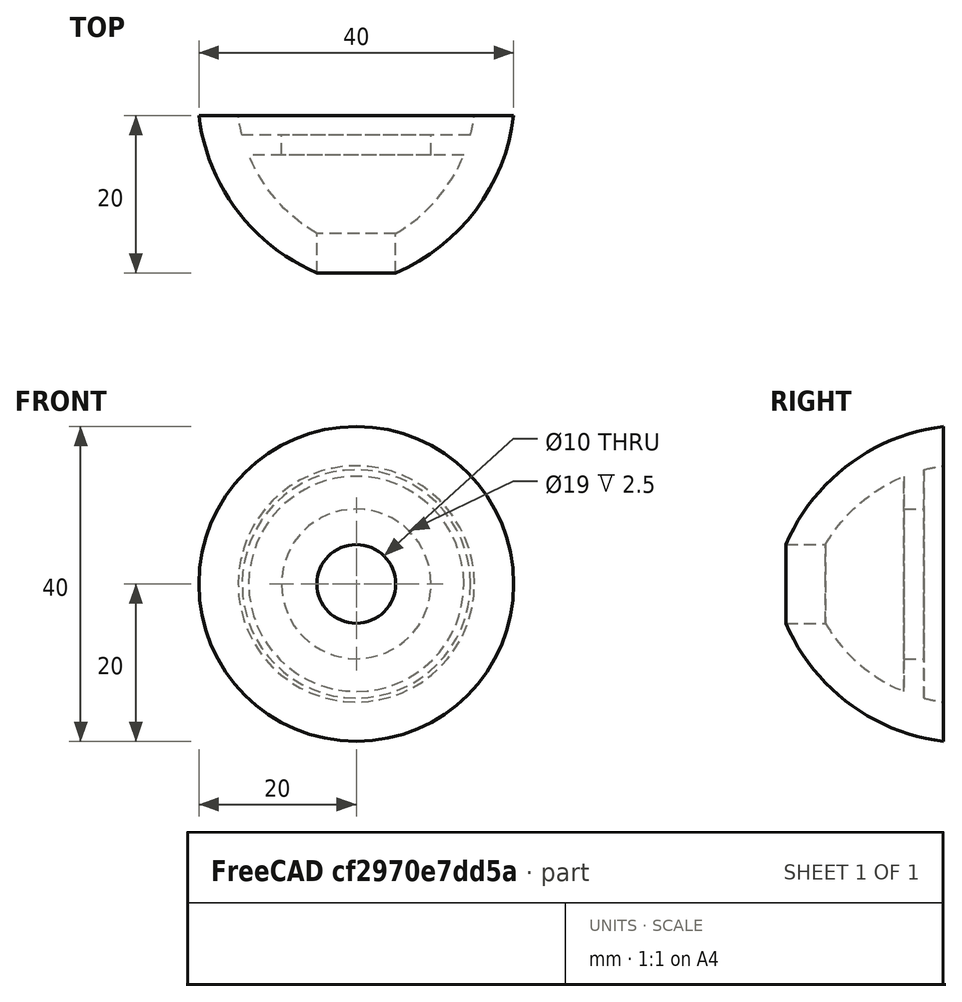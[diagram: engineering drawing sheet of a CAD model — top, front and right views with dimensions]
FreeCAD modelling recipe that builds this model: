
FCSTD DOCUMENT  (FreeCAD 0.18R4 (GitTag))
Label: Ariel Reciever
License: All rights reserved
LicenseURL: http://en.wikipedia.org/wiki/All_rights_reserved
objects: Sketcher::SketchObject×1, PartDesign::Revolution×1, PartDesign::Body×1, Mesh::Feature×1
note: 4 computed .brp shape members not serialized (recipe doc carries the construction recipe); baked Part::Feature solids carry a one-line shape summary decoded from their .brp

FEATURE [Sketcher::SketchObject] Sketch
  MapMode = 5
  Support = -> [XY_Plane]
  sketch-geometry (12):
    g0: ArcOfCircle CenterX=-4.82051 CenterY=22.9904 CenterZ=0 NormalX=0 NormalY=0 NormalZ=1 AngleXU=0 Radius=25 StartAngle=5.11609 EndAngle=6.16328
    g1: LineSegment StartX=5 StartY=-3.6e-15 StartZ=0 EndX=5 EndY=5 EndZ=0
    g2: LineSegment StartX=20 StartY=20 StartZ=0 EndX=15 EndY=20 EndZ=0
    g3: LineSegment [constr] StartX=0 StartY=26.4416 StartZ=0 EndX=26.4416 EndY=0 EndZ=0
    g4: GeomPoint X=12.9669 Y=13.4747 Z=0
    g5: GeomPoint X=16.5024 Y=9.93921 Z=0
    g6: LineSegment StartX=13.6625 StartY=15 StartZ=0 EndX=9.5 EndY=15 EndZ=0
    g7: LineSegment StartX=9.5 StartY=15 StartZ=0 EndX=9.5 EndY=17.5 EndZ=0
    g8: LineSegment StartX=9.5 StartY=17.5 StartZ=0 EndX=14.5 EndY=17.5 EndZ=0
    g9: ArcOfCircle [constr] CenterX=-5.42857 CenterY=22.7857 CenterZ=0 NormalX=0 NormalY=0 NormalZ=1 AngleXU=0 Radius=20.6176 StartAngle=5.24271 EndAngle=6.14766
    g10: ArcOfCircle CenterX=-5.42857 CenterY=22.7857 CenterZ=0 NormalX=0 NormalY=0 NormalZ=1 AngleXU=0 Radius=20.6176 StartAngle=5.24271 EndAngle=5.89596
    g11: ArcOfCircle CenterX=-5.42857 CenterY=22.7857 CenterZ=0 NormalX=0 NormalY=0 NormalZ=1 AngleXU=0 Radius=20.6176 StartAngle=6.02392 EndAngle=6.14766
  constraints (38):
    c: PointOnObject(g0,g-1)
    c: DistanceX(g-1,g0) = 5
    c: Radius(g0) = 25
    c: DistanceX(g-1,g0) = 20
    c: DistanceY(g-1,g0) = 20
    c: Coincident(g1,g0)
    c: Vertical(g1)
    c: Coincident(g2,g0)
    c: Horizontal(g2)
    c: DistanceX(g2,g2) = 5
    c: DistanceY(g1,g1) = 5
    c: PointOnObject(g3,g-2)
    c: PointOnObject(g3,g-1)
    c: Angle(g3,g-1) = 0.785398
    c: PointOnObject(g4,g3)
    c: PointOnObject(g5,g3)
    c: PointOnObject(g5,g0)
    c: Distance(g4,g5) = 5
    c: Coincident(g6,g7)
    c: Vertical(g7)
    c: Coincident(g7,g8)
    c: Horizontal(g8)
    c: Coincident(g9,g1)
    c: Coincident(g9,g2)
    c: PointOnObject(g4,g9)
    c: PointOnObject(g8,g9)
    c: PointOnObject(g6,g9)
    c: Horizontal(g6)
    c: DistanceX(g8,g8) = 5
    c: DistanceY(g7,g7) = 2.5
    c: DistanceY(g8,g2) = 2.5
    c: Coincident(g10,g1)
    c: Coincident(g10,g6)
    c: Tangent(g10,g9)
    c: Coincident(g11,g8)
    c: Coincident(g11,g2)
    c: Tangent(g11,g9)
    c: DistanceX(g-1,g8) = 14.5
FEATURE [PartDesign::Revolution] Revolution
  Angle = 360
  Axis = (0,1,0)
  Base = (0,0,0)
  Profile = -> Sketch
  ReferenceAxis = -> Sketch [V_Axis]
  Reversed = true
FEATURE [PartDesign::Body] Body
  Group = -> [Sketch,Revolution]
  Origin = -> Origin
  Tip = -> Revolution
FEATURE [Mesh::Feature] Mesh  label="Body (Meshed)"
